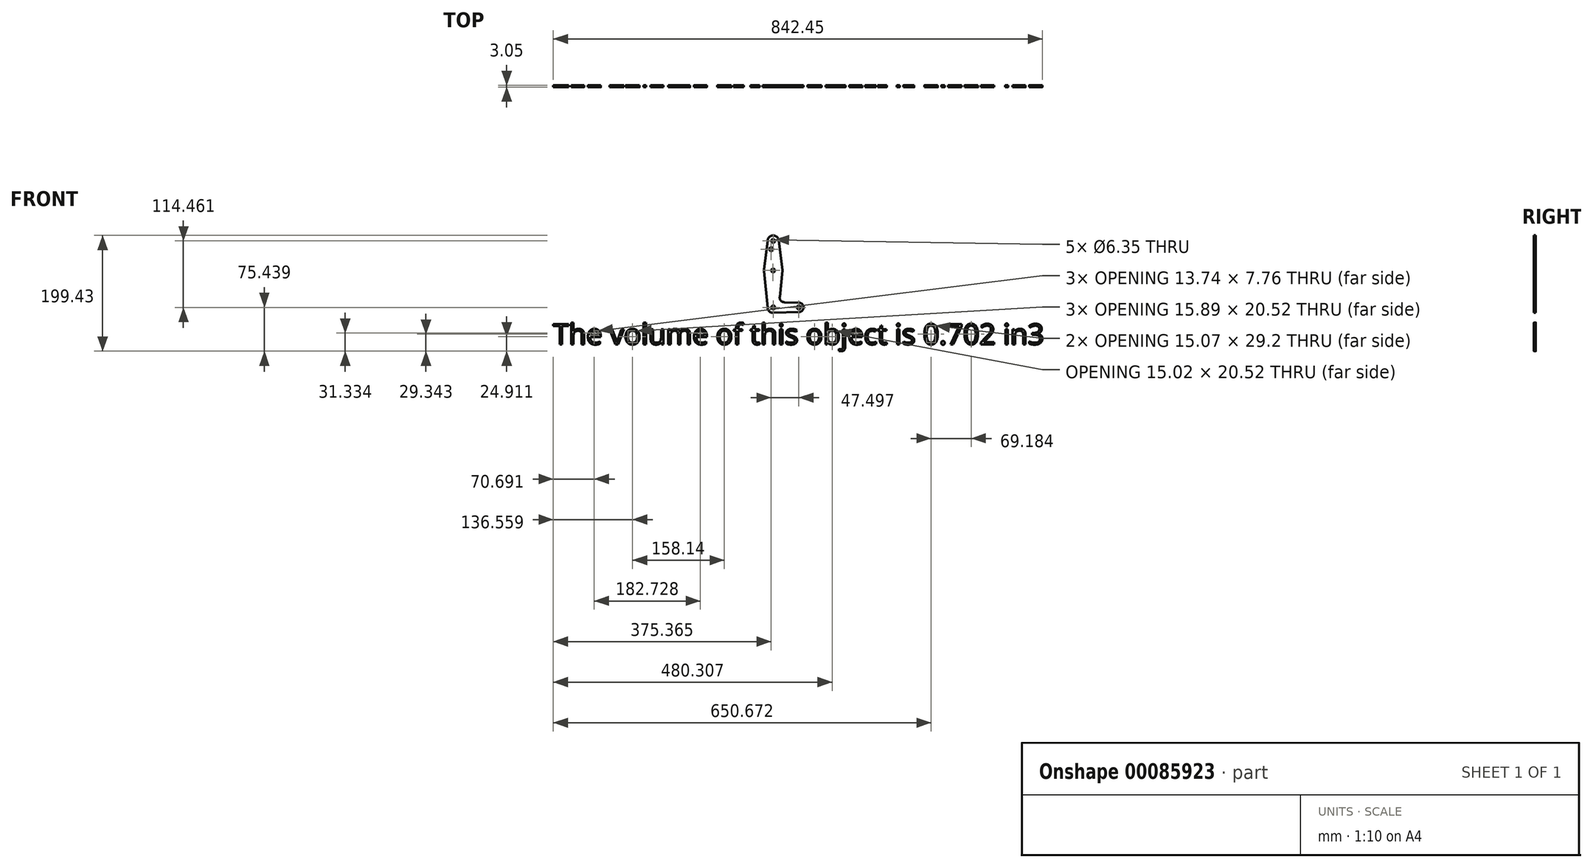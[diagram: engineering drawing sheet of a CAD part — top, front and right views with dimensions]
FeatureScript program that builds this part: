
annotation { "Feature Type Name" : "Feature", "Feature Type Description" : "" }
export const myFeature = defineFeature(function(context is Context, id is Id, definition is map)
    precondition{}
    {
        {
            var Q0;
            Q0=qCreatedBy(makeId("Front.planeOp"),FACE);
            var sketch = newSketch(context, id + "F0", { "sketchPlane" : qUnion([Q0])});
            skLineSegment(sketch, "E0", {"start": v(0, 50.8) * mm, "end": v(0, -63.5) * mm, "construction": true});
            skLineSegment(sketch, "E1", {"start": v(0, -63.5) * mm, "end": v(44.45, -63.5) * mm, "construction": true});
            skCircle(sketch, "E2", {"center": v(0, 50.8) * mm, "radius": 9.53 * mm});
            skCircle(sketch, "E3", {"center": v(0, 0) * mm, "radius": 15.88 * mm});
            skCircle(sketch, "E4", {"center": v(0, -63.5) * mm, "radius": 9.53 * mm});
            skCircle(sketch, "E5", {"center": v(44.45, -63.5) * mm, "radius": 7.94 * mm});
            skLineSegment(sketch, "E6", {"start": v(-9.52, 50.82) * mm, "end": v(-16, 0) * mm});
            skLineSegment(sketch, "E7", {"start": v(9.4, 52.34) * mm, "end": v(16, 0) * mm});
            skLineSegment(sketch, "E8", {"start": v(16, 0) * mm, "end": v(11.35, -45.9) * mm});
            skLineSegment(sketch, "E9", {"start": v(-9.52, -63.73) * mm, "end": v(-15.8, -1.6) * mm});
            skLineSegment(sketch, "E10", {"start": v(18.98, -54.65) * mm, "end": v(44.73, -55.57) * mm});
            skLineSegment(sketch, "E11", {"start": v(0, -73.03) * mm, "end": v(44.73, -71.43) * mm});
            skCircle(sketch, "E12", {"center": v(0, 50.8) * mm, "radius": 3.18 * mm});
            skCircle(sketch, "E13", {"center": v(0.06, -63.62) * mm, "radius": 3.18 * mm});
            skCircle(sketch, "E14", {"center": v(-0.12, 0) * mm, "radius": 3.18 * mm});
            skCircle(sketch, "E15", {"center": v(44.14, -63.66) * mm, "radius": 3.18 * mm});
            skCircle(sketch, "E16", {"center": v(-3.36, 36.53) * mm, "radius": 3.18 * mm});
            skPoint(sketch, "E17.newPointB", {"position": v(0, -53.98) * mm});
            skArc(sketch, "E17.filletArc", {"start": v(11.35, -45.9) * mm, "mid": v(13.27, -51.93) * mm, "end": v(18.98, -54.65) * mm});
            skText(sketch, "E18", { "text": "The volume of this object is 0.702 in3", "fontName": "OpenSans-Regular.ttf"});
            const initialGuessF0  = {"E18": [-0.37915, -0.1273, 1, 0, 0.03534]};
            skSetInitialGuess(sketch, initialGuessF0);
            skSolve(sketch);
        }
        {
            var Q0;
            Q0=makeQuery(id+"F0.imprint","IMPRINT",FACE,{"disambiguationData":[TD([[makeQuery(id+"F0.imprint","IMPRINT",EDGE,{"derivedFrom":sQuery(id+"F0.wireOp",EDGE,"E12")}),-1.0]])]});
            var Q1;
            Q1=makeQuery(id+"F0.imprint","IMPRINT",FACE,{"disambiguationData":[TD([[makeQuery(id+"F0.imprint","IMPRINT",EDGE,{"derivedFrom":sQuery(id+"F0.wireOp",EDGE,"E16")}),-1.0]])]});
            var Q2;
            Q2=makeQuery(id+"F0.imprint","IMPRINT",FACE,{"disambiguationData":[TD([[makeQuery(id+"F0.imprint","IMPRINT",EDGE,{"derivedFrom":sQuery(id+"F0.wireOp",EDGE,"E14")}),-1.0]])]});
            var Q3;
            {var subQ0=sQuery(id+"F0.wireOp",EDGE,"E8");Q3=makeQuery(id+"F0.imprint","IMPRINT",FACE,{"disambiguationData":[TD([[makeQuery(id+"F0.imprint","IMPRINT",EDGE,{"derivedFrom":subQ0}),-1.0]])]});}
            var Q4;
            Q4=makeQuery(id+"F0.imprint","IMPRINT",FACE,{"disambiguationData":[TD([[makeQuery(id+"F0.imprint","IMPRINT",EDGE,{"derivedFrom":sQuery(id+"F0.wireOp",EDGE,"E13")}),-1.0]])]});
            var Q5;
            Q5=makeQuery(id+"F0.imprint","IMPRINT",FACE,{"disambiguationData":[TD([[makeQuery(id+"F0.imprint","IMPRINT",EDGE,{"derivedFrom":sQuery(id+"F0.wireOp",EDGE,"E15")}),-1.0]])]});
            extrude(context, id + "F1", {"entities" : qUnion([Q0, Q1, Q2, Q3, Q4, Q5]), "depth" : 3.05 * mm});
        }
        {
            var Q0;
            Q0 = qSketchRegion(id + "F0", true);
            extrude(context, id + "F2", {"entities" : qUnion([Q0]), "operationType" : NewBodyOperationType.ADD, "depth" : 3.05 * mm});
        }
    });
